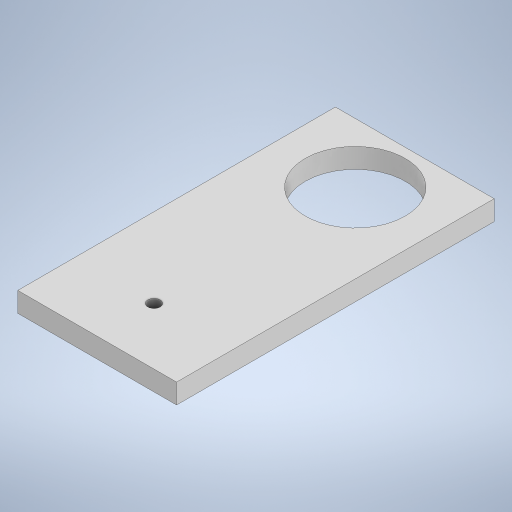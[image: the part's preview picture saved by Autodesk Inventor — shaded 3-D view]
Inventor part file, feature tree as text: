
AUTODESK INVENTOR PART (.ipt)
format: ipt  version: 2024 (Build 280153000, 153)  size: 224,768 bytes
history: native  units: in
note: dims shown in document units (in); Inventor stores cm internally (conversion verified against a paired STEP export)
features: extrude x2, sketch x2
ambient origin geometry x8: Origin, YZ Plane, XZ Plane, XY Plane, X Axis, Y Axis, Z Axis, Center Point
bodies: Solid1 (feature_tree)
feature tree (4):
  extrude  "Extrusion1"  Depth=2.0in
  extrude  "Extrusion2"  Depth=0.125in
  sketch  "Sketch1"  dims[d0=1.0in d1=2.0in]
  sketch  "Sketch2"  dims[d2=0.125in d3=0.0in d4=0.0787in d5=0.3578in d6=0.5in d7=0.6299in d8=0.375in d9=0.5in d10=0.125in d11=0.0in]
